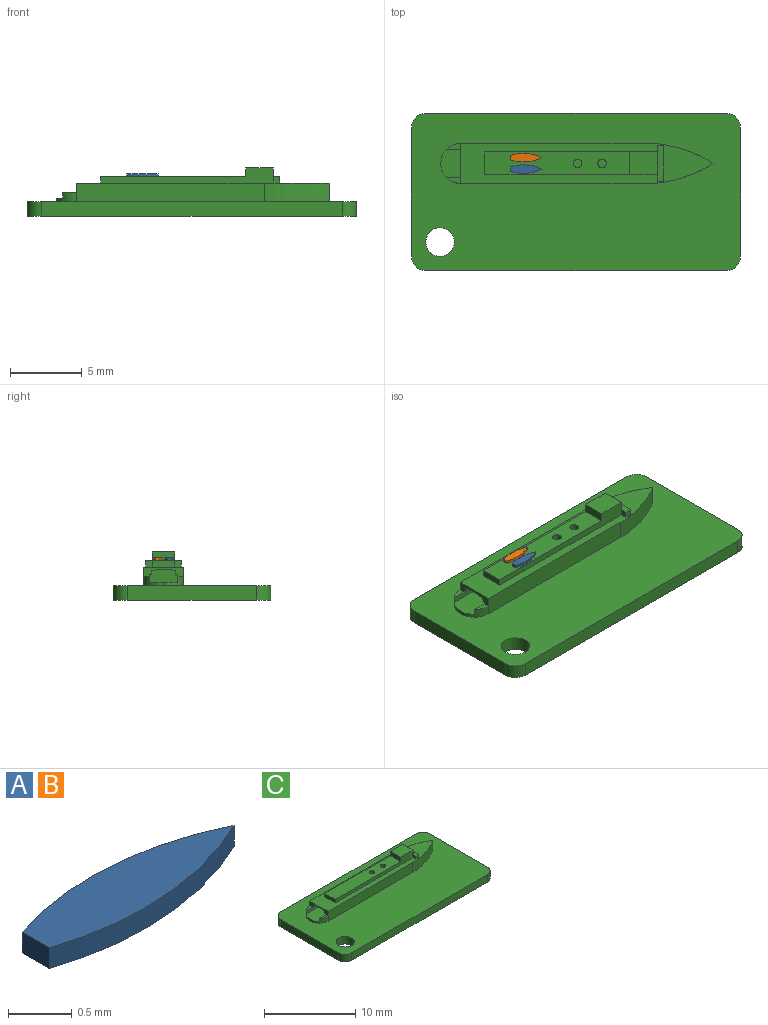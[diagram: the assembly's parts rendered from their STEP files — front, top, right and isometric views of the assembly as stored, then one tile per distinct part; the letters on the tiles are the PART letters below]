
ASSEMBLY  parts=3 mates=2
PART A: 5 faces, bbox 2.2x0.6x0.2 mm
  f0: plane 0.3x0.2mm, normal (-1,0,0), area 0.1mm2, adj f1,f2,f3,f4
  f1: cylinder r=2.89mm len=2.2mm, axis (0,0,-1), area 0.5mm2, adj f0,f2,f3,f4
  f2: cylinder r=2.89mm len=2.2mm, axis (0,0,-1), area 0.5mm2, adj f0,f1,f3,f4
  f3: plane 2.2x0.6mm, normal (0,0,1), area 1mm2, adj f0,f1,f2
  f4: plane 2.2x0.6mm, normal (0,0,-1), area 1mm2, adj f0,f1,f2
PART B: same geometry as A
PART C: 48 faces, bbox 23x11x3.4 mm
  f0: plane 10.11x1.6mm, normal (0,0,1), area 15.6mm2, adj f21,f27,f28,f41,f44,f46
  f1: plane 2.5x0.46mm, normal (0,0,1), area 1.1mm2, adj f21,f22,f23,f24,f25,f26,f27,f42
  f2: plane 0.97x0.4mm, normal (0,0,1), area 0.3mm2, adj f4,f30,f39
  f3: cylinder r=1.38mm len=1.4mm, axis (0,0,-1), area 1mm2, adj f4,f6,f17,f29,f31,f32
  f4: cylinder r=1.38mm len=1.4mm, axis (0,0,-1), area 1mm2, adj f2,f3,f6,f18,f31,f39
  f5: plane 17.65x2.82mm, normal (0,0,1), area 24.8mm2, adj f17,f18,f19,f20,f21,f22,f23,f24
  f6: plane 23x11mm, normal (0,0,1), area 200.8mm2, adj f3,f4,f7,f8,f9,f10,f11,f12
  f7: plane 9x1mm, normal (1,0,0), area 9mm2, adj f6,f8,f14,f15
  f8: cylinder r=1mm len=1mm, axis (0,0,1), area 1.6mm2, adj f6,f7,f9,f15
  f9: plane 21x1mm, normal (0,1,0), area 21mm2, adj f6,f8,f10,f15
  f10: cylinder r=1mm len=1mm, axis (0,0,1), area 1.6mm2, adj f6,f9,f11,f15
  f11: plane 9x1mm, normal (-1,0,0), area 9mm2, adj f6,f10,f12,f15
  f12: cylinder r=1mm len=1mm, axis (0,0,1), area 1.6mm2, adj f6,f11,f13,f15
  f13: plane 21x1mm, normal (0,-1,0), area 21mm2, adj f6,f12,f14,f15
  f14: cylinder r=1mm len=1mm, axis (0,0,1), area 1.6mm2, adj f6,f7,f13,f15
  f15: plane 23x11mm, normal (0,0,-1), area 249mm2, adj f7,f8,f9,f10,f11,f12,f13,f14
  f16: cylinder r=1mm len=2mm, axis (0,0,1), area 6.3mm2, adj f6,f15
  f17: plane 13.11x1.3mm, normal (0,1,0), area 17mm2, adj f3,f5,f6,f20,f30
  f18: plane 13.11x1.3mm, normal (0,-1,0), area 17mm2, adj f4,f5,f6,f19,f30
  f19: extruded ~4.54x1.4mm, area 6.3mm2, adj f5,f6,f18,f20
  f20: extruded ~4.54x1.4mm, area 6.3mm2, adj f5,f6,f17,f19
  f21: plane 12.06x1.06mm, normal (0,-1,0), area 6.7mm2, adj f0,f1,f5,f22,f28,f41,f42,f43
  f22: plane 0.46x0.45mm, normal (-1,0,0), area 0.2mm2, adj f1,f5,f21,f23
  f23: plane 0.46x0.46mm, normal (0,-1,0), area 0.2mm2, adj f1,f5,f22,f24
  f24: plane 2.5x0.46mm, normal (1,0,0), area 1.2mm2, adj f1,f5,f23,f25
  f25: plane 0.46x0.46mm, normal (0,1,0), area 0.2mm2, adj f1,f5,f24,f26
  f26: plane 0.46x0.45mm, normal (-1,0,0), area 0.2mm2, adj f1,f5,f25,f27
  f27: plane 12.06x1.06mm, normal (0,1,0), area 6.7mm2, adj f0,f1,f5,f26,f28,f41,f42,f43
  f28: plane 1.6x0.46mm, normal (-1,0,0), area 0.7mm2, adj f0,f5,f21,f27
  f29: plane 0.97x0.4mm, normal (0,0,1), area 0.3mm2, adj f3,f30,f32
  f30: plane 2.8x0.65mm, normal (-1,0,0), area 1mm2, adj f2,f5,f17,f18,f29,f32,f33,f34
  f31: plane 2.38x2mm, normal (0,0,1), area 4.5mm2, adj f3,f4,f32,f39,f40
  f32: plane 1.97x0.56mm, normal (0,-1,0), area 0.9mm2, adj f3,f29,f30,f31,f38,f40
  f33: plane 1x0.15mm, normal (0,0,-1), area 0.2mm2, adj f30,f34,f39,f40
  f34: plane 1x0.23mm, normal (0,1,0), area 0.2mm2, adj f30,f33,f35,f40
  f35: cylinder r=2.86mm len=1mm, axis (-1,0,0), area 0.9mm2, adj f30,f34,f36,f40
  f36: cylinder r=2.86mm len=1mm, axis (-1,0,0), area 0.9mm2, adj f30,f35,f37,f40
  f37: plane 1x0.23mm, normal (0,-1,0), area 0.2mm2, adj f30,f36,f38,f40
  f38: plane 1x0.15mm, normal (0,0,-1), area 0.2mm2, adj f30,f32,f37,f40
  f39: plane 1.97x0.56mm, normal (0,1,0), area 0.9mm2, adj f2,f4,f30,f31,f33,f40
  f40: plane 2x0.89mm, normal (-1,0,0), area 1.6mm2, adj f31,f32,f33,f34,f35,f36,f37,f38
  f41: plane 1.6x0.6mm, normal (-1,0,0), area 1mm2, adj f0,f21,f27,f43
  f42: plane 1.6x0.6mm, normal (1,0,0), area 1mm2, adj f1,f21,f27,f43
  f43: plane 1.95x1.6mm, normal (0,0,1), area 3.1mm2, adj f21,f27,f41,f42
  f44: cylinder r=0.3mm len=1.76mm, axis (0,0,-1), area 3.3mm2, adj f0,f45
  f45: plane 0.6x0.6mm, normal (0,0,1), area 0.3mm2, adj f44
  f46: cylinder r=0.3mm len=1.76mm, axis (0,0,-1), area 3.3mm2, adj f0,f47
  f47: plane 0.6x0.6mm, normal (0,0,1), area 0.3mm2, adj f46
PLACE A t=(2.88,-15.39,-2.92)mm
PLACE B t=(2.88,-14.59,-2.92)mm
PLACE C t=(-0.64,-5.8,-2.98)mm
MATE fastened B.f4 <-> C.f0  axis (0,0,-1) through (-4.24,-5.4,-1.22)mm
MATE fastened A.f4 <-> C.f0  axis (0,0,-1) through (-4.24,-6.2,-1.22)mm
